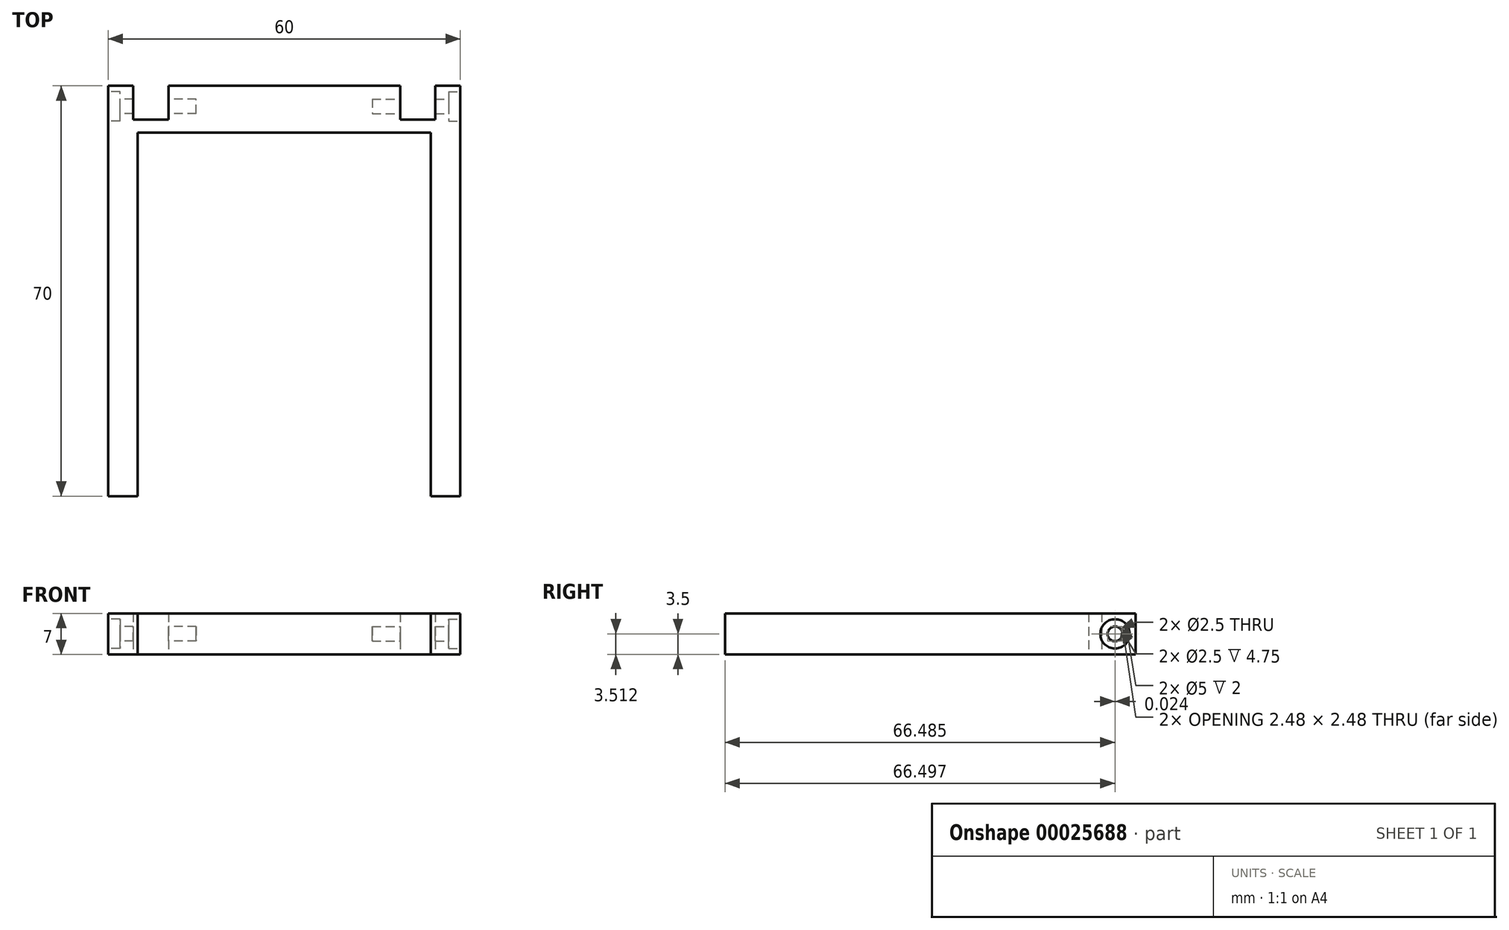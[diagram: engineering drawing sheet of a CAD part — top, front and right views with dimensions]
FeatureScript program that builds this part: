
annotation { "Feature Type Name" : "Feature", "Feature Type Description" : "" }
export const myFeature = defineFeature(function(context is Context, id is Id, definition is map)
    precondition{}
    {
        {
            var Q0;
            Q0=qCreatedBy(makeId("Top.planeOp"),FACE);
            var sketch = newSketch(context, id + "F0", { "sketchPlane" : qUnion([Q0])});
            skLineSegment(sketch, "E0.bottom", {"start": v(-29.28, -5.36) * mm, "end": v(-24.28, -5.36) * mm});
            skLineSegment(sketch, "E0.top", {"start": v(-29.28, 64.64) * mm, "end": v(-25.03, 64.64) * mm});
            skLineSegment(sketch, "E0.left", {"start": v(-29.28, -5.36) * mm, "end": v(-29.28, 64.64) * mm});
            skLineSegment(sketch, "E0.right", {"start": v(30.72, -5.36) * mm, "end": v(30.72, 64.64) * mm});
            skLineSegment(sketch, "E1.top", {"start": v(-24.28, 56.64) * mm, "end": v(25.72, 56.64) * mm});
            skLineSegment(sketch, "E1.left", {"start": v(-24.28, -5.36) * mm, "end": v(-24.28, 56.64) * mm});
            skLineSegment(sketch, "E1.right", {"start": v(25.72, -5.36) * mm, "end": v(25.72, 56.64) * mm});
            skLineSegment(sketch, "E2.trimOffspring", {"start": v(25.72, -5.36) * mm, "end": v(30.72, -5.36) * mm});
            skLineSegment(sketch, "E3", {"start": v(-25.03, 64.64) * mm, "end": v(-25.03, 58.89) * mm});
            skLineSegment(sketch, "E4", {"start": v(-25.03, 58.89) * mm, "end": v(-19.03, 58.89) * mm});
            skLineSegment(sketch, "E5", {"start": v(-19.03, 58.89) * mm, "end": v(-19.03, 64.64) * mm});
            skLineSegment(sketch, "E6.trimOffspring", {"start": v(-19.03, 64.64) * mm, "end": v(20.47, 64.64) * mm});
            skLineSegment(sketch, "E7", {"start": v(0.72, 56.64) * mm, "end": v(0.72, 64.64) * mm, "construction": true});
            skLineSegment(sketch, "E8.MirrorCS", {"start": v(20.47, 64.64) * mm, "end": v(20.47, 64.64) * mm});
            skLineSegment(sketch, "E9.MirrorCS", {"start": v(20.47, 64.64) * mm, "end": v(-19.03, 64.64) * mm});
            skLineSegment(sketch, "E10.MirrorCS", {"start": v(20.47, 58.89) * mm, "end": v(20.47, 64.64) * mm});
            skLineSegment(sketch, "E11.MirrorCS", {"start": v(30.72, 64.64) * mm, "end": v(26.47, 64.64) * mm});
            skLineSegment(sketch, "E12.MirrorCS", {"start": v(26.47, 64.64) * mm, "end": v(26.47, 58.89) * mm});
            skLineSegment(sketch, "E13.MirrorCS", {"start": v(26.47, 58.89) * mm, "end": v(20.47, 58.89) * mm});
            skLineSegment(sketch, "E14.trimOffspring", {"start": v(26.47, 64.64) * mm, "end": v(30.72, 64.64) * mm});
            skLineSegment(sketch, "E15.trimOffspring", {"start": v(-25.03, 64.64) * mm, "end": v(-29.28, 64.64) * mm});
            skLineSegment(sketch, "E16", {"start": v(-29.28, 61.14) * mm, "end": v(0.72, 61.14) * mm, "construction": true});
            skLineSegment(sketch, "E17", {"start": v(-22.03, 58.89) * mm, "end": v(-22.03, 69.46) * mm, "construction": true});
            skSolve(sketch);
        }
        {
            var Q0;
            Q0=makeQuery(id+"F0.imprint","IMPRINT",FACE,{"disambiguationData":[TD([[makeQuery(id+"F0.imprint","IMPRINT",EDGE,{"derivedFrom":sQuery(id+"F0.wireOp",EDGE,"E0.bottom")}),1.0]])]});
            extrude(context, id + "F1", {"entities" : qUnion([Q0]), "depth" : 7 * mm});
        }
        {
            var Q0;
            Q0=makeQuery(id+"F1.opExtrude","SWEPT_FACE",FACE,{"disambiguationData":[OSD([sQuery(id+"F0.wireOp",EDGE,"E0.left")])]});
            var sketch = newSketch(context, id + "F2", { "sketchPlane" : qUnion([Q0])});
            skLineSegment(sketch, "E18", {"start": v(-64.64, 3.5) * mm, "end": v(-52.4, 3.5) * mm, "construction": true});
            skCircle(sketch, "E19", {"center": v(-61.14, 3.5) * mm, "radius": 2.5 * mm});
            skCircle(sketch, "E20", {"center": v(-61.14, 3.5) * mm, "radius": 1.25 * mm});
            skSolve(sketch);
        }
        {
            var Q0;
            Q0=makeQuery(id+"F2.imprint","IMPRINT",FACE,{"disambiguationData":[TD([[makeQuery(id+"F2.imprint","IMPRINT",EDGE,{"derivedFrom":sQuery(id+"F2.wireOp",EDGE,"E20")}),1.0]])]});
            extrude(context, id + "F3", {"entities" : qUnion([Q0]), "operationType" : NewBodyOperationType.REMOVE, "oppositeDirection" : true, "depth" : 15 * mm});
        }
        {
            var Q0;
            Q0=makeQuery(id+"F2.imprint","IMPRINT",FACE,{"disambiguationData":[TD([[makeQuery(id+"F2.imprint","IMPRINT",EDGE,{"derivedFrom":sQuery(id+"F2.wireOp",EDGE,"E19")}),1.0]])]});
            extrude(context, id + "F4", {"entities" : qUnion([Q0]), "operationType" : NewBodyOperationType.REMOVE, "oppositeDirection" : true, "depth" : 2 * mm});
        }
        {
            var Q0;
            Q0=makeQuery(id+"F1.opExtrude","SWEPT_FACE",FACE,{"disambiguationData":[OSD([sQuery(id+"F0.wireOp",EDGE,"E0.right")])]});
            var sketch = newSketch(context, id + "F5", { "sketchPlane" : qUnion([Q0])});
            skLineSegment(sketch, "E21", {"start": v(27.51, 3.5) * mm, "end": v(64.64, 3.5) * mm, "construction": true});
            skCircle(sketch, "E22", {"center": v(61.14, 3.5) * mm, "radius": 2.5 * mm});
            skCircle(sketch, "E23", {"center": v(61.14, 3.5) * mm, "radius": 1.25 * mm});
            skSolve(sketch);
        }
        {
            var Q0;
            Q0=makeQuery(id+"F5.imprint","IMPRINT",FACE,{"disambiguationData":[TD([[makeQuery(id+"F5.imprint","IMPRINT",EDGE,{"derivedFrom":sQuery(id+"F5.wireOp",EDGE,"E23")}),1.0]])]});
            extrude(context, id + "F6", {"entities" : qUnion([Q0]), "operationType" : NewBodyOperationType.REMOVE, "oppositeDirection" : true, "depth" : 15 * mm});
        }
        {
            var Q0;
            Q0 = qSketchRegion(id + "F5", true);
            extrude(context, id + "F7", {"entities" : qUnion([Q0]), "operationType" : NewBodyOperationType.REMOVE, "oppositeDirection" : true, "depth" : 2 * mm});
        }
    });
